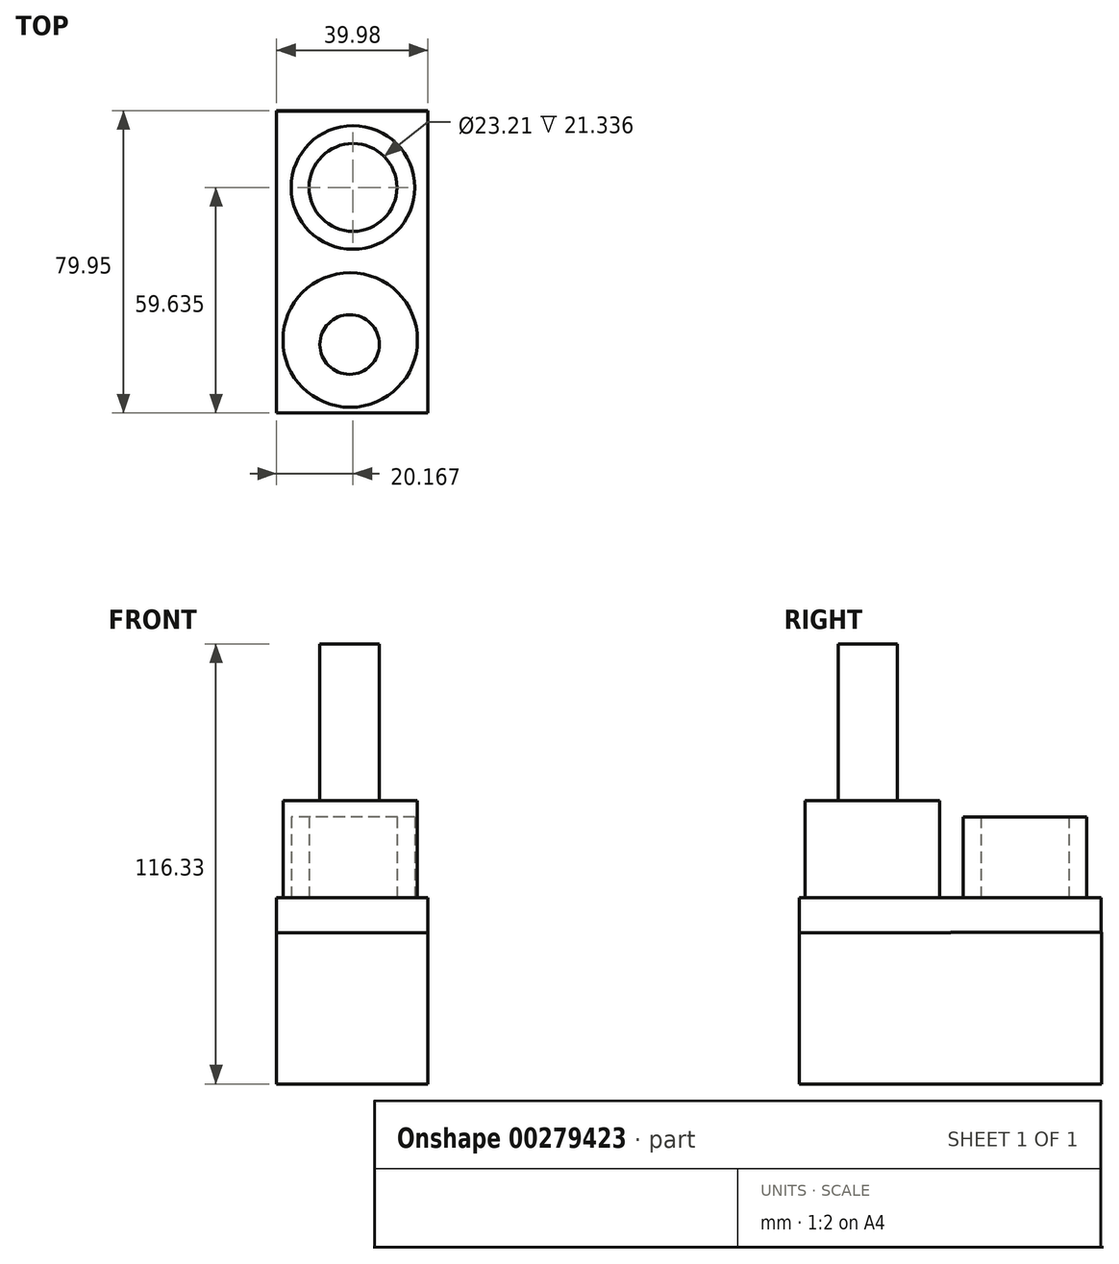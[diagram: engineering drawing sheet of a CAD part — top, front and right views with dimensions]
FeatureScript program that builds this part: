
annotation { "Feature Type Name" : "Feature", "Feature Type Description" : "" }
export const myFeature = defineFeature(function(context is Context, id is Id, definition is map)
    precondition{}
    {
        {
            var Q0;
            Q0=qCreatedBy(makeId("Top.planeOp"),FACE);
            var sketch = newSketch(context, id + "F0", { "sketchPlane" : qUnion([Q0])});
            skLineSegment(sketch, "E0.bottom", {"start": v(0, 0) * mm, "end": v(39.98, 0) * mm});
            skLineSegment(sketch, "E0.top", {"start": v(0, 39.97) * mm, "end": v(39.98, 39.97) * mm});
            skLineSegment(sketch, "E0.left", {"start": v(0, 0) * mm, "end": v(0, 39.97) * mm});
            skLineSegment(sketch, "E0.right", {"start": v(39.98, 0) * mm, "end": v(39.98, 39.97) * mm});
            skSolve(sketch);
        }
        {
            var Q0;
            Q0 = qSketchRegion(id + "F0", true);
            extrude(context, id + "F1", {"entities" : qUnion([Q0]), "depth" : 40.03 * mm});
        }
        {
            var Q0;
            Q0=qCreatedBy(makeId("Top.planeOp"),FACE);
            var sketch = newSketch(context, id + "F2", { "sketchPlane" : qUnion([Q0])});
            skCircle(sketch, "E1", {"center": v(20.17, 19.66) * mm, "radius": 11.6 * mm});
            skCircle(sketch, "E2", {"center": v(20.17, 19.66) * mm, "radius": 16.34 * mm});
            skSolve(sketch);
        }
        {
            var Q0;
            Q0 = qSketchRegion(id + "F2", true);
            extrude(context, id + "F3", {"entities" : qUnion([Q0]), "operationType" : NewBodyOperationType.ADD, "depth" : 70.61 * mm});
        }
        {
            var Q0;
            Q0=qCreatedBy(makeId("Top.planeOp"),FACE);
            var sketch = newSketch(context, id + "F4", { "sketchPlane" : qUnion([Q0])});
            skLineSegment(sketch, "E3.bottom", {"start": v(0, 0) * mm, "end": v(39.98, 0) * mm});
            skLineSegment(sketch, "E3.top", {"start": v(0, -39.98) * mm, "end": v(39.98, -39.98) * mm});
            skLineSegment(sketch, "E3.left", {"start": v(0, 0) * mm, "end": v(0, -39.98) * mm});
            skLineSegment(sketch, "E3.right", {"start": v(39.98, 0) * mm, "end": v(39.98, -39.98) * mm});
            skSolve(sketch);
        }
        {
            var Q0;
            Q0 = qSketchRegion(id + "F4", true);
            extrude(context, id + "F5", {"entities" : qUnion([Q0]), "operationType" : NewBodyOperationType.ADD, "depth" : 39.98 * mm});
        }
        {
            var Q0;
            Q0=qCreatedBy(makeId("Top.planeOp"),FACE);
            var sketch = newSketch(context, id + "F6", { "sketchPlane" : qUnion([Q0])});
            skCircle(sketch, "E4", {"center": v(19.44, -20.68) * mm, "radius": 17.78 * mm});
            skSolve(sketch);
        }
        {
            var Q0;
            Q0 = qSketchRegion(id + "F6", true);
            extrude(context, id + "F7", {"entities" : qUnion([Q0]), "operationType" : NewBodyOperationType.ADD, "depth" : 74.93 * mm});
        }
        {
            var Q0;
            Q0=qCreatedBy(makeId("Top.planeOp"),FACE);
            var sketch = newSketch(context, id + "F8", { "sketchPlane" : qUnion([Q0])});
            skLineSegment(sketch, "E5.bottom", {"start": v(0, 0) * mm, "end": v(39.9, 0) * mm});
            skLineSegment(sketch, "E5.top", {"start": v(0, 39.82) * mm, "end": v(39.9, 39.82) * mm});
            skLineSegment(sketch, "E5.left", {"start": v(0, 0) * mm, "end": v(0, 39.82) * mm});
            skLineSegment(sketch, "E5.right", {"start": v(39.9, 0) * mm, "end": v(39.9, 39.82) * mm});
            skLineSegment(sketch, "E6.top", {"start": v(0, -39.97) * mm, "end": v(39.9, -39.97) * mm});
            skLineSegment(sketch, "E6.left", {"start": v(0, 0) * mm, "end": v(0, -39.97) * mm});
            skLineSegment(sketch, "E6.right", {"start": v(39.9, 0) * mm, "end": v(39.9, -39.97) * mm});
            skSolve(sketch);
        }
        {
            var Q0;
            Q0 = qSketchRegion(id + "F8", true);
            extrude(context, id + "F9", {"entities" : qUnion([Q0]), "operationType" : NewBodyOperationType.ADD, "depth" : 49.28 * mm});
        }
        {
            var Q0;
            Q0=qCreatedBy(makeId("Top.planeOp"),FACE);
            var sketch = newSketch(context, id + "F10", { "sketchPlane" : qUnion([Q0])});
            skCircle(sketch, "E7", {"center": v(19.3, -21.85) * mm, "radius": 7.87 * mm});
            skSolve(sketch);
        }
        {
            var Q0;
            Q0 = qSketchRegion(id + "F10", true);
            extrude(context, id + "F11", {"entities" : qUnion([Q0]), "operationType" : NewBodyOperationType.ADD, "depth" : 116.33 * mm});
        }
    });
